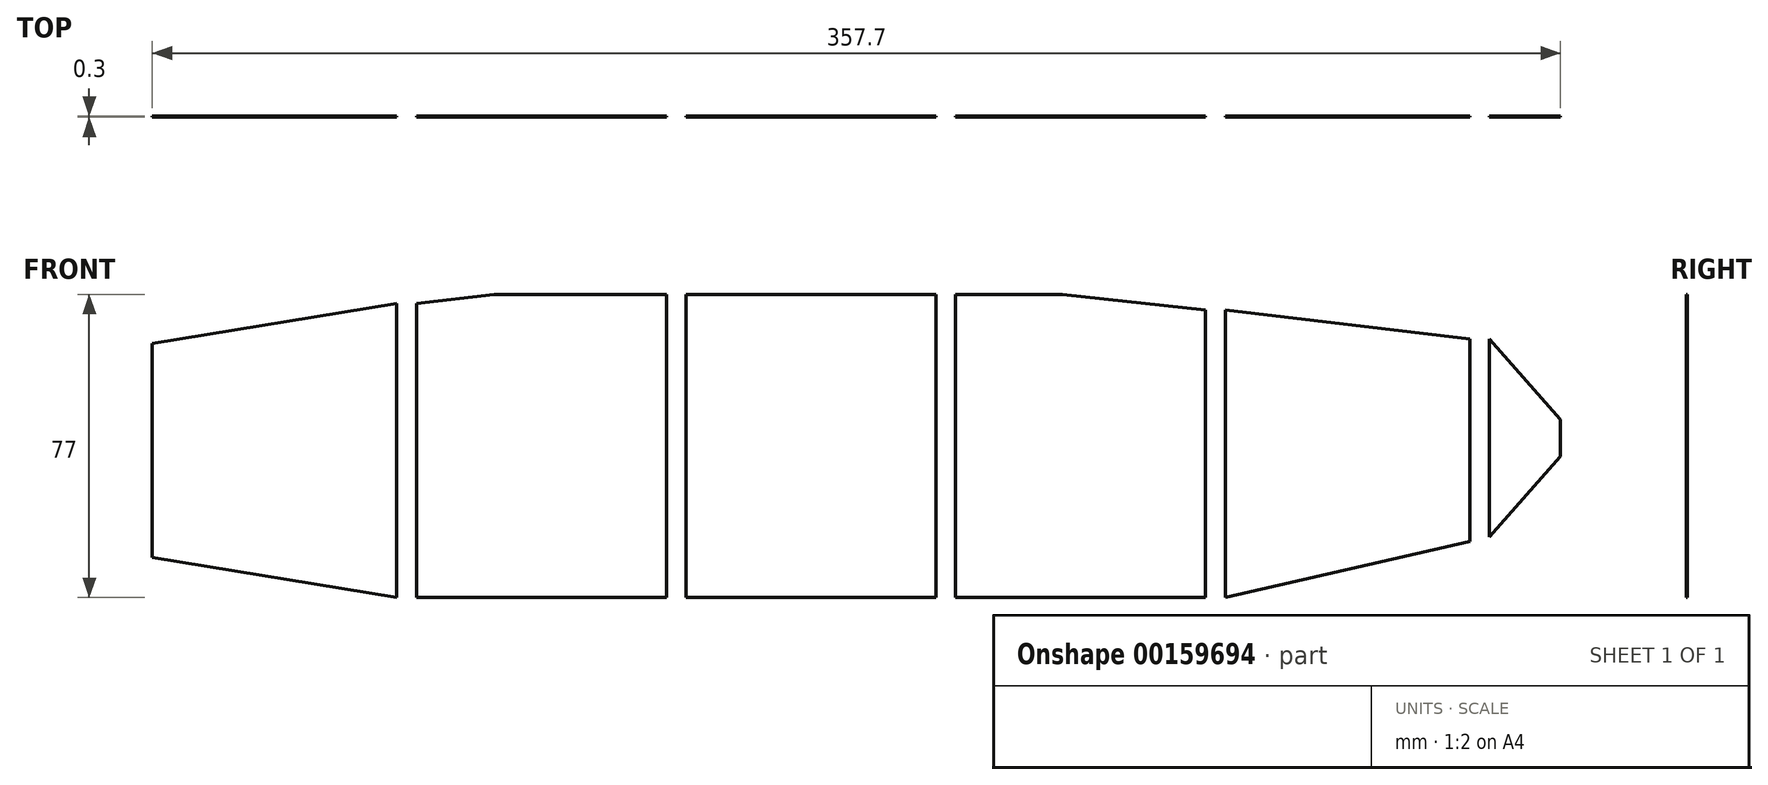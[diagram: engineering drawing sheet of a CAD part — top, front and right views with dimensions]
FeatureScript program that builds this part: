
annotation { "Feature Type Name" : "Feature", "Feature Type Description" : "" }
export const myFeature = defineFeature(function(context is Context, id is Id, definition is map)
    precondition{}
    {
        {
            var Q0;
            Q0=qCreatedBy(makeId("Front.planeOp"),FACE);
            var sketch = newSketch(context, id + "F0", { "sketchPlane" : qUnion([Q0])});
            skLineSegment(sketch, "E0", {"start": v(-16.33, 32.57) * mm, "end": v(-16.33, -40.43) * mm});
            skLineSegment(sketch, "E1", {"start": v(-16.33, -40.43) * mm, "end": v(45.77, -26.23) * mm});
            skLineSegment(sketch, "E2", {"start": v(45.77, -26.23) * mm, "end": v(45.77, 25.27) * mm});
            skLineSegment(sketch, "E3", {"start": v(45.77, 25.27) * mm, "end": v(-16.33, 32.57) * mm});
            skLineSegment(sketch, "E4", {"start": v(-21.33, 32.57) * mm, "end": v(-21.33, -40.43) * mm});
            skLineSegment(sketch, "E5", {"start": v(-21.33, -40.43) * mm, "end": v(-84.83, -40.43) * mm});
            skLineSegment(sketch, "E6", {"start": v(-84.83, -40.43) * mm, "end": v(-84.83, 36.57) * mm});
            skLineSegment(sketch, "E7", {"start": v(-84.83, 36.57) * mm, "end": v(-57.73, 36.57) * mm});
            skLineSegment(sketch, "E8", {"start": v(-57.73, 36.57) * mm, "end": v(-21.33, 32.57) * mm});
            skLineSegment(sketch, "E9.0", {"start": v(-89.83, -40.43) * mm, "end": v(-89.83, 36.57) * mm});
            skLineSegment(sketch, "E10", {"start": v(-89.83, 36.57) * mm, "end": v(-153.33, 36.57) * mm});
            skLineSegment(sketch, "E11", {"start": v(-153.33, 36.57) * mm, "end": v(-153.33, -40.43) * mm});
            skLineSegment(sketch, "E12", {"start": v(-153.33, -40.43) * mm, "end": v(-89.83, -40.43) * mm});
            skLineSegment(sketch, "E13.0", {"start": v(-158.33, 36.57) * mm, "end": v(-158.33, -40.43) * mm});
            skLineSegment(sketch, "E14", {"start": v(-158.33, -40.43) * mm, "end": v(-221.83, -40.43) * mm});
            skLineSegment(sketch, "E15", {"start": v(-221.83, -40.43) * mm, "end": v(-221.83, 34.27) * mm});
            skLineSegment(sketch, "E16", {"start": v(-221.83, 34.27) * mm, "end": v(-202.13, 36.57) * mm});
            skLineSegment(sketch, "E17", {"start": v(-202.13, 36.57) * mm, "end": v(-158.33, 36.57) * mm});
            skLineSegment(sketch, "E18", {"start": v(39.44, -60.43) * mm, "end": v(-272.72, -60.43) * mm});
            skLineSegment(sketch, "E19.0", {"start": v(-226.83, -40.43) * mm, "end": v(-226.83, 34.27) * mm});
            skLineSegment(sketch, "E20.0", {"start": v(-288.93, -30.28) * mm, "end": v(-288.93, 24.12) * mm});
            skLineSegment(sketch, "E21", {"start": v(-226.83, 34.27) * mm, "end": v(-288.93, 24.12) * mm});
            skLineSegment(sketch, "E22", {"start": v(-288.93, -30.28) * mm, "end": v(-226.83, -40.43) * mm});
            skPoint(sketch, "E23.end.orphan", {"position": v(-288.93, -3.08) * mm});
            skPoint(sketch, "E23.start.orphan", {"position": v(-226.83, -3.08) * mm});
            skLineSegment(sketch, "E24.0", {"start": v(50.77, -25.03) * mm, "end": v(50.77, 25.27) * mm});
            skLineSegment(sketch, "E25", {"start": v(68.77, 0.12) * mm, "end": v(68.77, 0.12) * mm});
            skLineSegment(sketch, "E26", {"start": v(68.77, 4.82) * mm, "end": v(68.77, -4.58) * mm});
            skLineSegment(sketch, "E27", {"start": v(50.77, 25.27) * mm, "end": v(68.77, 4.82) * mm});
            skLineSegment(sketch, "E28", {"start": v(68.77, -4.58) * mm, "end": v(50.77, -25.03) * mm});
            skPoint(sketch, "E29.start.orphan", {"position": v(50.77, 0.12) * mm});
            skSolve(sketch);
        }
        {
            var Q0;
            Q0=makeQuery(id+"F0.imprint","IMPRINT",FACE,{"disambiguationData":[TD([[makeQuery(id+"F0.imprint","IMPRINT",EDGE,{"derivedFrom":sQuery(id+"F0.wireOp",EDGE,"E0")}),1.0]])]});
            var Q1;
            Q1=makeQuery(id+"F0.imprint","IMPRINT",FACE,{"disambiguationData":[TD([[makeQuery(id+"F0.imprint","IMPRINT",EDGE,{"derivedFrom":sQuery(id+"F0.wireOp",EDGE,"E24.0")}),-1.0]])]});
            var Q2;
            Q2=makeQuery(id+"F0.imprint","IMPRINT",FACE,{"disambiguationData":[TD([[makeQuery(id+"F0.imprint","IMPRINT",EDGE,{"derivedFrom":sQuery(id+"F0.wireOp",EDGE,"E19.0")}),1.0]])]});
            var Q3;
            Q3=makeQuery(id+"F0.imprint","IMPRINT",FACE,{"disambiguationData":[TD([[makeQuery(id+"F0.imprint","IMPRINT",EDGE,{"derivedFrom":sQuery(id+"F0.wireOp",EDGE,"E13.0")}),-1.0]])]});
            var Q4;
            Q4=makeQuery(id+"F0.imprint","IMPRINT",FACE,{"disambiguationData":[TD([[makeQuery(id+"F0.imprint","IMPRINT",EDGE,{"derivedFrom":sQuery(id+"F0.wireOp",EDGE,"E9.0")}),1.0]])]});
            var Q5;
            Q5=makeQuery(id+"F0.imprint","IMPRINT",FACE,{"disambiguationData":[TD([[makeQuery(id+"F0.imprint","IMPRINT",EDGE,{"derivedFrom":sQuery(id+"F0.wireOp",EDGE,"E4")}),-1.0]])]});
            extrude(context, id + "F1", {"entities" : qUnion([Q0, Q1, Q2, Q3, Q4, Q5]), "depth" : 0.3 * mm});
        }
    });
